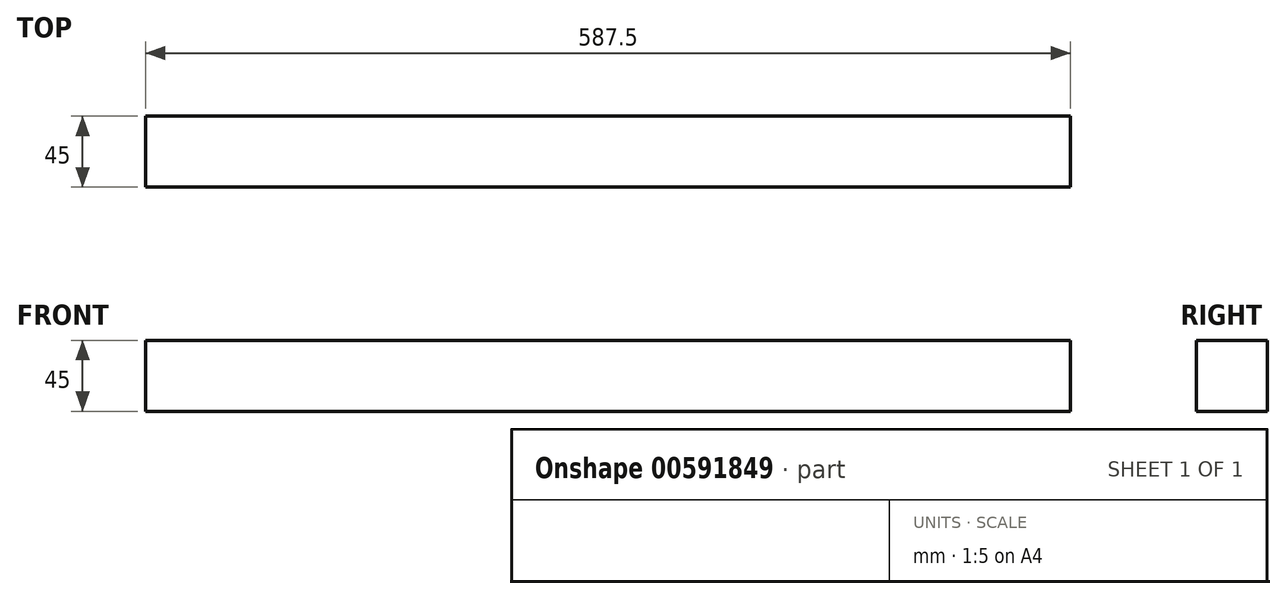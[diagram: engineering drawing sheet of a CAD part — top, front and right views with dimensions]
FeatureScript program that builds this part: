
annotation { "Feature Type Name" : "Feature", "Feature Type Description" : "" }
export const myFeature = defineFeature(function(context is Context, id is Id, definition is map)
    precondition{}
    {
        {
            var Q0;
            Q0=qCreatedBy(makeId("Right.planeOp"),FACE);
            var sketch = newSketch(context, id + "F0", { "sketchPlane" : qUnion([Q0])});
            skLineSegment(sketch, "E0.bottom", {"start": v(0, 0) * mm, "end": v(45, 0) * mm});
            skLineSegment(sketch, "E0.top", {"start": v(0, 45) * mm, "end": v(45, 45) * mm});
            skLineSegment(sketch, "E0.left", {"start": v(0, 0) * mm, "end": v(0, 45) * mm});
            skLineSegment(sketch, "E0.right", {"start": v(45, 0) * mm, "end": v(45, 45) * mm});
            skSolve(sketch);
        }
        {
            var Q0;
            Q0=makeQuery(id+"F0.imprint","IMPRINT",FACE,{"disambiguationData":[TD([[makeQuery(id+"F0.imprint","IMPRINT",EDGE,{"derivedFrom":sQuery(id+"F0.wireOp",EDGE,"E0.bottom")}),1.0]])]});
            extrude(context, id + "F1", {"entities" : qUnion([Q0]), "depth" : 587.5 * mm, "offsetDistance" : 25 * mm});
        }
    });
